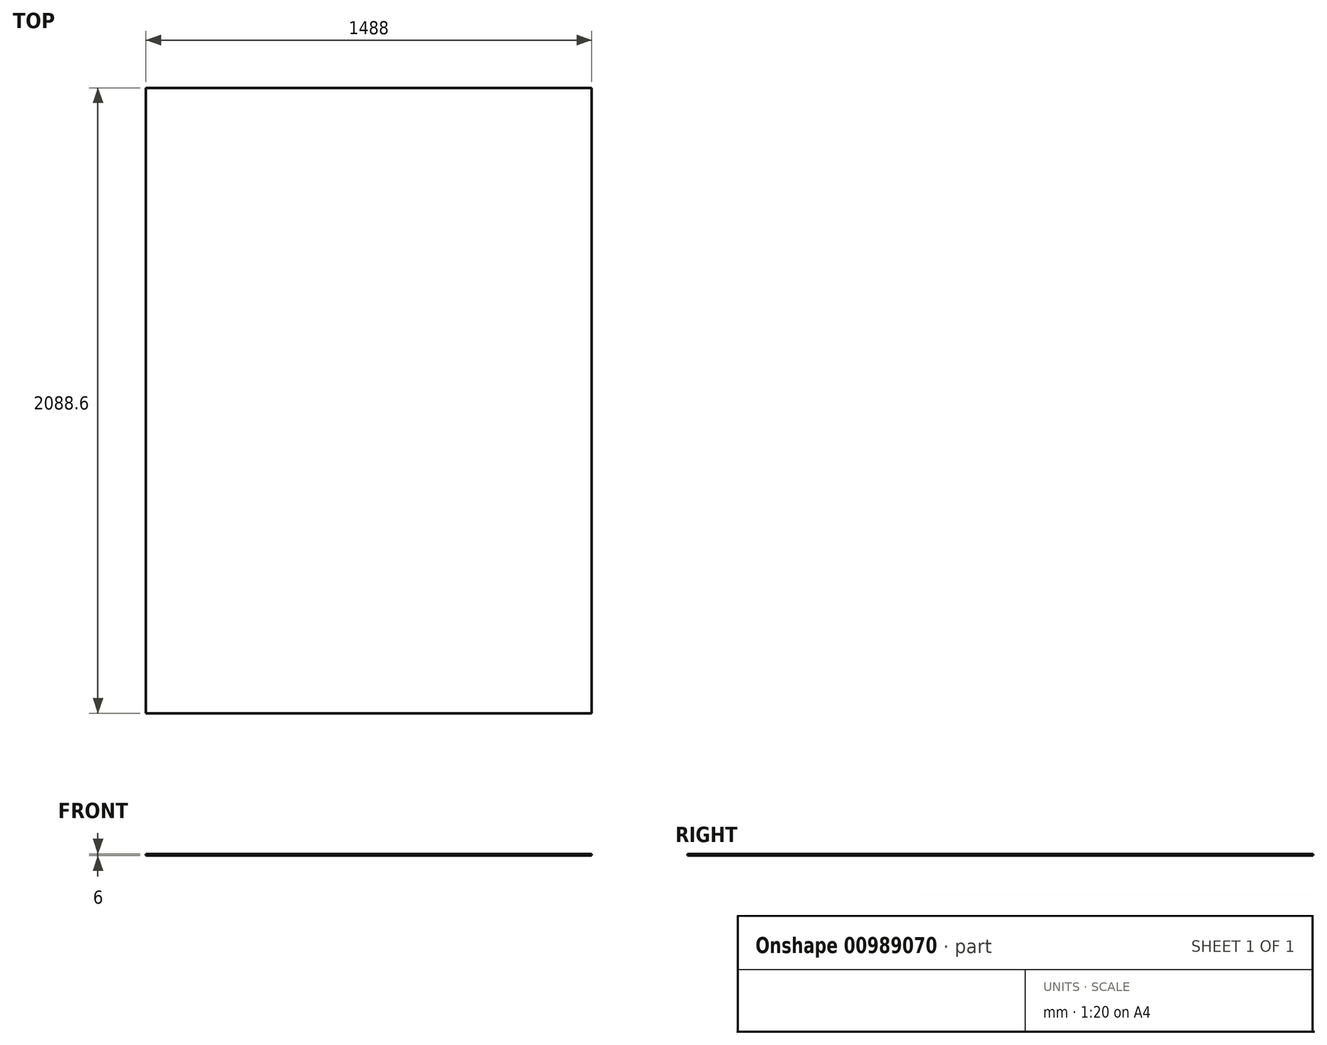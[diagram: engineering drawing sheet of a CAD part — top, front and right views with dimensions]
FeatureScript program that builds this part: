
annotation { "Feature Type Name" : "Feature", "Feature Type Description" : "" }
export const myFeature = defineFeature(function(context is Context, id is Id, definition is map)
    precondition{}
    {
        {
            var Q0;
            Q0=qCreatedBy(makeId("Top.planeOp"),FACE);
            var sketch = newSketch(context, id + "F0", { "sketchPlane" : qUnion([Q0])});
            skLineSegment(sketch, "E0.bottom", {"start": v(744, 1044.3) * mm, "end": v(-744, 1044.3) * mm});
            skLineSegment(sketch, "E0.top", {"start": v(744, -1044.3) * mm, "end": v(-744, -1044.3) * mm});
            skLineSegment(sketch, "E0.left", {"start": v(744, 1044.3) * mm, "end": v(744, -1044.3) * mm});
            skLineSegment(sketch, "E0.right", {"start": v(-744, 1044.3) * mm, "end": v(-744, -1044.3) * mm});
            skPoint(sketch, "E0.middle", {"position": v(0, 0) * mm});
            skSolve(sketch);
        }
        {
            var Q0;
            Q0=makeQuery(id+"F0.imprint","IMPRINT",FACE,{"disambiguationData":[TD([[makeQuery(id+"F0.imprint","IMPRINT",EDGE,{"derivedFrom":sQuery(id+"F0.wireOp",EDGE,"E0.bottom")}),1.0]])]});
            extrude(context, id + "F1", {"entities" : qUnion([Q0]), "depth" : 6 * mm, "offsetDistance" : 25 * mm});
        }
    });
